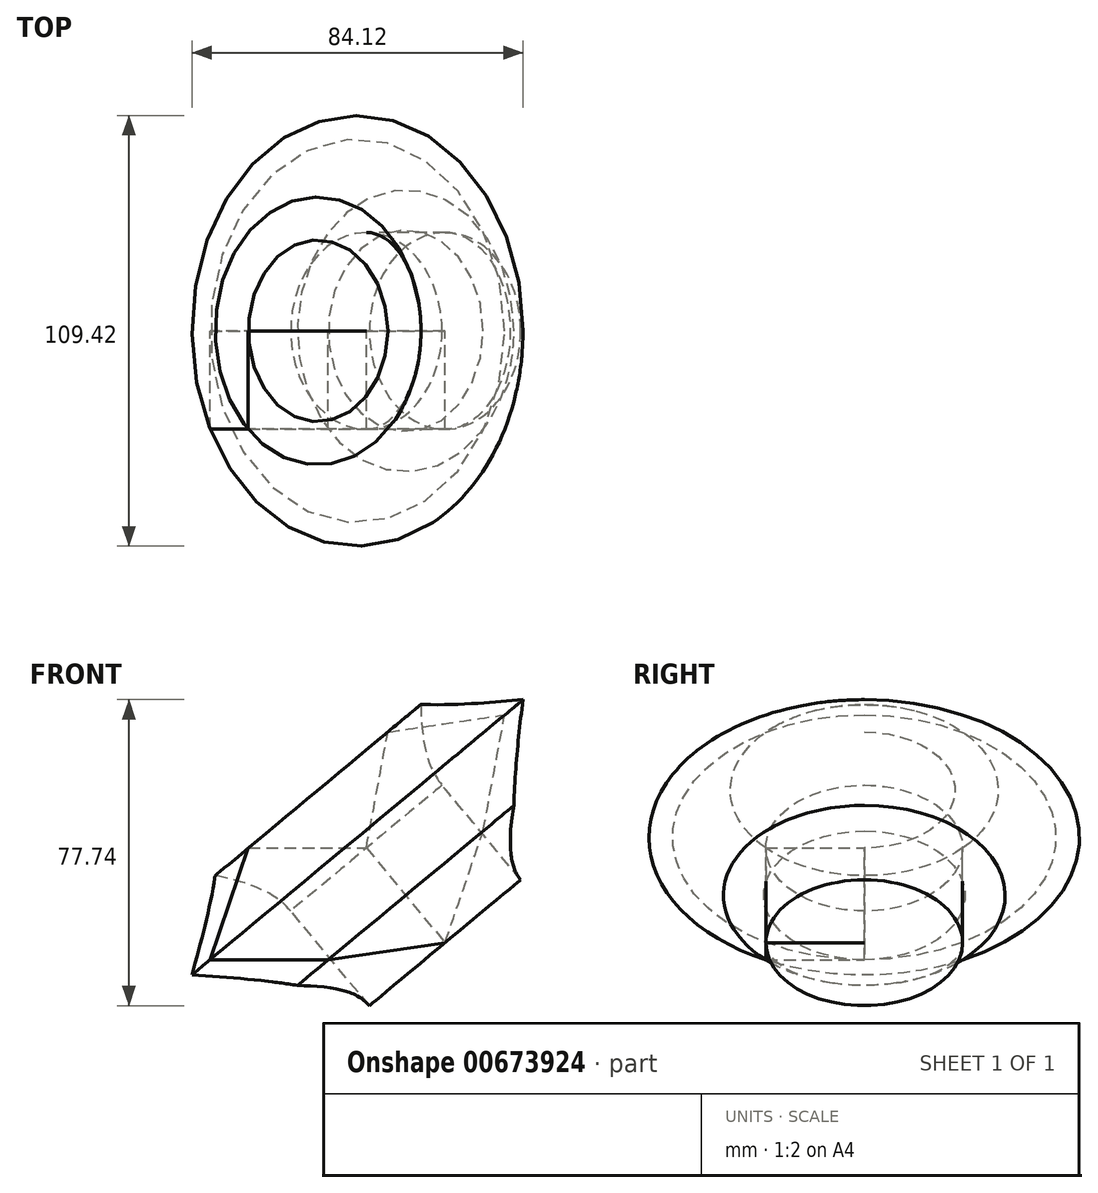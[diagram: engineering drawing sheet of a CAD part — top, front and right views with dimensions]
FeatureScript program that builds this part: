
annotation { "Feature Type Name" : "Feature", "Feature Type Description" : "" }
export const myFeature = defineFeature(function(context is Context, id is Id, definition is map)
    precondition{}
    {
        {
            var Q0;
            Q0=qCreatedBy(makeId("Front.planeOp"),FACE);
            var sketch = newSketch(context, id + "F0", { "sketchPlane" : qUnion([Q0])});
            skLineSegment(sketch, "E0", {"start": v(0, 0) * mm, "end": v(-30, 0) * mm});
            skLineSegment(sketch, "E1", {"start": v(-30, 0) * mm, "end": v(-20.32, 28.4) * mm});
            skLineSegment(sketch, "E2", {"start": v(-20.32, 28.4) * mm, "end": v(9.68, 28.4) * mm});
            skLineSegment(sketch, "E3", {"start": v(9.68, 28.4) * mm, "end": v(29.68, 4.35) * mm});
            skLineSegment(sketch, "E4", {"start": v(29.68, 4.35) * mm, "end": v(0, 0) * mm});
            skSolve(sketch);
        }
        {
            var Q0;
            Q0 = qSketchRegion(id + "F0", true);
            extrude(context, id + "F1", {"entities" : qUnion([Q0]), "depth" : 25 * mm, "offsetDistance" : 25 * mm});
        }
        {
            var Q0;
            Q0 = qSketchRegion(id + "F0", true);
            var Q1;
            Q1=makeQuery(id+"F1.opExtrude","SWEPT_FACE",FACE,{"disambiguationData":[OSD([sQuery(id+"F0.wireOp",EDGE,"E3")])]});
            var Q2;
            Q2=makeQuery(id+"F1.opExtrude","CAP_FACE",FACE,{"disambiguationData":[OSD([sQuery(id+"F0.wireOp",EDGE,"E0"),sQuery(id+"F0.wireOp",EDGE,"E1"),sQuery(id+"F0.wireOp",EDGE,"E2"),sQuery(id+"F0.wireOp",EDGE,"E3"),sQuery(id+"F0.wireOp",EDGE,"E4")])],"isStart":false});
            var Q3;
            Q3=sQuery(id+"F0.wireOp",EDGE,"E3");
            revolve(context, id + "F2", {"entities" : qUnion([Q0, Q1, Q2]), "axis" : qUnion([Q3]), "revolveType" : RevolveType.FULL});
        }
    });
